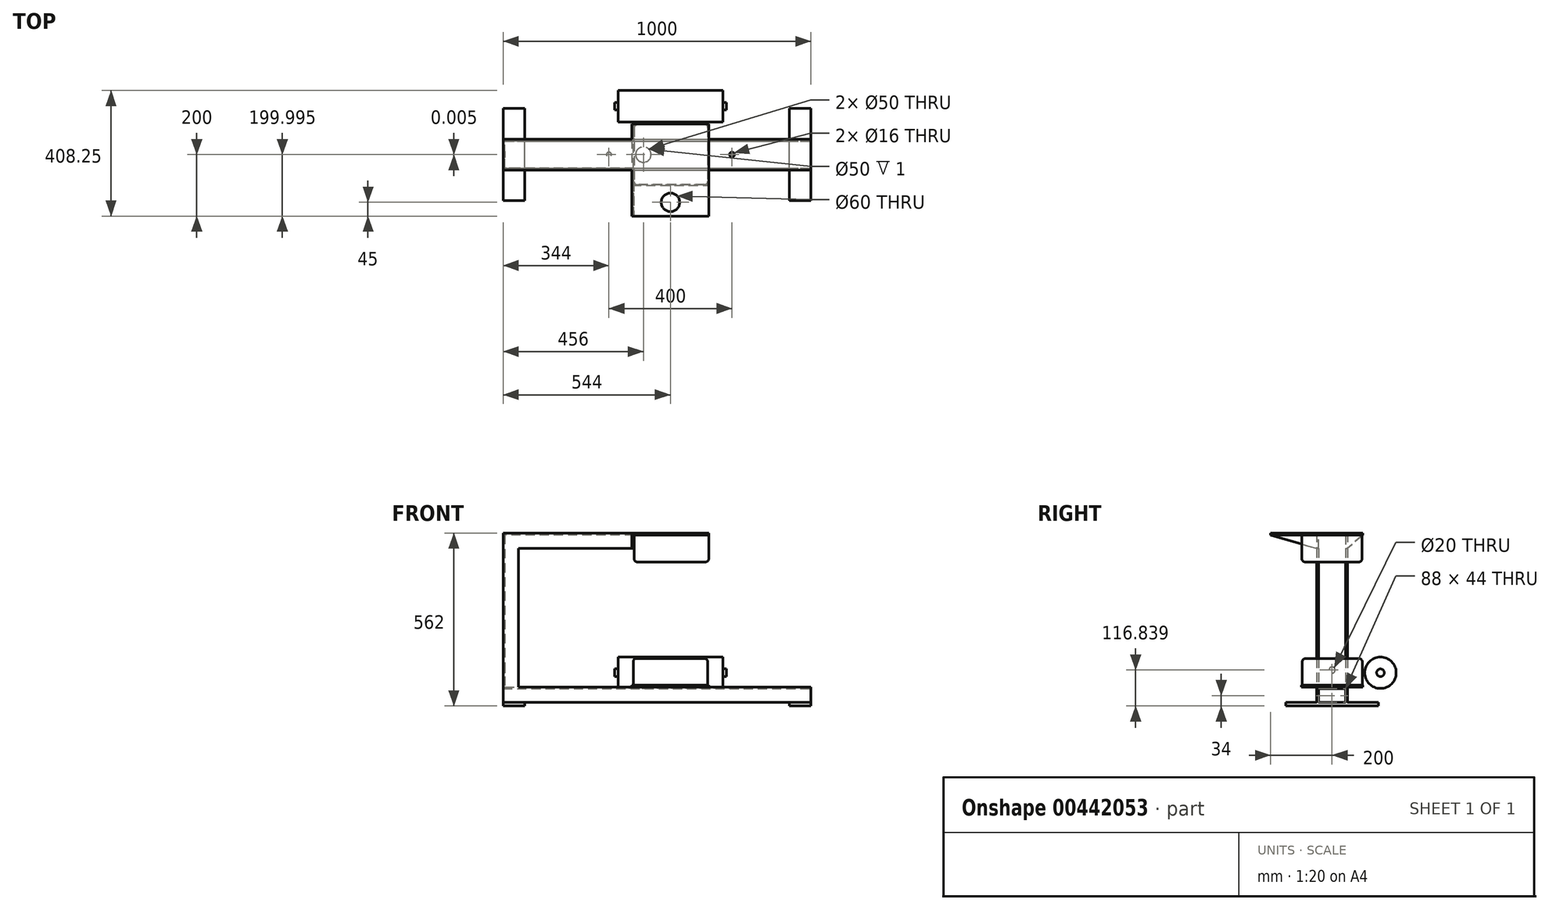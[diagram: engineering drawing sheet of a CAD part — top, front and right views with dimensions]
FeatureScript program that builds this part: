
annotation { "Feature Type Name" : "Feature", "Feature Type Description" : "" }
export const myFeature = defineFeature(function(context is Context, id is Id, definition is map)
    precondition{}
    {
        {
            var Q0;
            Q0=qCreatedBy(makeId("Right.planeOp"),FACE);
            var sketch = newSketch(context, id + "F0", { "sketchPlane" : qUnion([Q0])});
            skLineSegment(sketch, "E0", {"start": v(50, 0) * mm, "end": v(50, 50) * mm});
            skLineSegment(sketch, "E1", {"start": v(50, 50) * mm, "end": v(-50, 50) * mm});
            skLineSegment(sketch, "E2", {"start": v(-50, 50) * mm, "end": v(-50, 0) * mm});
            skLineSegment(sketch, "E3", {"start": v(-50, 0) * mm, "end": v(-44, 0) * mm});
            skLineSegment(sketch, "E4", {"start": v(-44, 0) * mm, "end": v(-44, 44) * mm});
            skLineSegment(sketch, "E5", {"start": v(-44, 44) * mm, "end": v(44, 44) * mm});
            skLineSegment(sketch, "E6", {"start": v(44, 44) * mm, "end": v(44, 0) * mm});
            skLineSegment(sketch, "E7", {"start": v(44, 0) * mm, "end": v(50, 0) * mm});
            skSolve(sketch);
        }
        {
            var Q0;
            Q0 = qSketchRegion(id + "F0", true);
            extrude(context, id + "F1", {"entities" : qUnion([Q0]), "oppositeDirection" : true, "depth" : 1000 * mm});
        }
        {
            var Q0;
            Q0=makeQuery(id+"F1.opExtrude","SWEPT_FACE",FACE,{"disambiguationData":[OSD([sQuery(id+"F0.wireOp",EDGE,"E1")])]});
            var sketch = newSketch(context, id + "F2", { "sketchPlane" : qUnion([Q0])});
            skLineSegment(sketch, "E8", {"start": v(-1000, 50) * mm, "end": v(-1000, -50) * mm});
            skLineSegment(sketch, "E9", {"start": v(-1000, -50) * mm, "end": v(-950, -50) * mm});
            skLineSegment(sketch, "E10", {"start": v(-950, -50) * mm, "end": v(-950, -44) * mm});
            skLineSegment(sketch, "E11", {"start": v(-950, -44) * mm, "end": v(-994, -44) * mm});
            skLineSegment(sketch, "E12", {"start": v(-994, -44) * mm, "end": v(-994, 44) * mm});
            skLineSegment(sketch, "E13", {"start": v(-994, 44) * mm, "end": v(-950, 44) * mm});
            skLineSegment(sketch, "E14", {"start": v(-950, 44) * mm, "end": v(-950, 50) * mm});
            skLineSegment(sketch, "E15", {"start": v(-950, 50) * mm, "end": v(-1000, 50) * mm});
            skSolve(sketch);
        }
        {
            var Q0;
            Q0=makeQuery(id+"F2.imprint","IMPRINT",FACE,{"disambiguationData":[TD([[makeQuery(id+"F2.imprint","IMPRINT",EDGE,{"derivedFrom":sQuery(id+"F2.wireOp",EDGE,"E8")}),1.0]])]});
            extrude(context, id + "F3", {"entities" : qUnion([Q0]), "operationType" : NewBodyOperationType.ADD, "depth" : 500 * mm});
        }
        {
            var Q0;
            Q0=makeQuery(id+"F3.opExtrude","SWEPT_FACE",FACE,{"disambiguationData":[OSD([sQuery(id+"F2.wireOp",EDGE,"E14")])]});
            var sketch = newSketch(context, id + "F4", { "sketchPlane" : qUnion([Q0])});
            skLineSegment(sketch, "E16", {"start": v(50, 550) * mm, "end": v(-50, 550) * mm});
            skLineSegment(sketch, "E17", {"start": v(-50, 550) * mm, "end": v(-50, 500) * mm});
            skLineSegment(sketch, "E18", {"start": v(-50, 500) * mm, "end": v(-44, 500) * mm});
            skLineSegment(sketch, "E19", {"start": v(-44, 500) * mm, "end": v(-44, 544) * mm});
            skLineSegment(sketch, "E20", {"start": v(-44, 544) * mm, "end": v(44, 544) * mm});
            skLineSegment(sketch, "E21", {"start": v(44, 544) * mm, "end": v(44, 500) * mm});
            skLineSegment(sketch, "E22", {"start": v(44, 500) * mm, "end": v(50, 500) * mm});
            skLineSegment(sketch, "E23", {"start": v(50, 500) * mm, "end": v(50, 550) * mm});
            skSolve(sketch);
        }
        {
            var Q0;
            Q0 = qSketchRegion(id + "F4", true);
            extrude(context, id + "F5", {"entities" : qUnion([Q0]), "operationType" : NewBodyOperationType.ADD, "depth" : 369 * mm, "hasSecondDirection" : true, "secondDirectionOppositeDirection" : true, "secondDirectionDepth" : 50 * mm});
        }
        {
            var Q0;
            Q0=makeQuery(id+"F5.opExtrude","CAP_FACE",FACE,{"disambiguationData":[OSD([sQuery(id+"F4.wireOp",EDGE,"E16"),sQuery(id+"F4.wireOp",EDGE,"E17"),sQuery(id+"F4.wireOp",EDGE,"E18"),sQuery(id+"F4.wireOp",EDGE,"E19"),sQuery(id+"F4.wireOp",EDGE,"E20"),sQuery(id+"F4.wireOp",EDGE,"E21"),sQuery(id+"F4.wireOp",EDGE,"E22"),sQuery(id+"F4.wireOp",EDGE,"E23")])],"isStart":false});
            var sketch = newSketch(context, id + "F6", { "sketchPlane" : qUnion([Q0])});
            skLineSegment(sketch, "E24", {"start": v(0, 550) * mm, "end": v(100, 550) * mm});
            skLineSegment(sketch, "E25", {"start": v(100, 550) * mm, "end": v(100, 544) * mm});
            skLineSegment(sketch, "E26", {"start": v(100, 544) * mm, "end": v(-200, 544) * mm});
            skLineSegment(sketch, "E27", {"start": v(-200, 544) * mm, "end": v(-200, 550) * mm});
            skLineSegment(sketch, "E28", {"start": v(-200, 550) * mm, "end": v(0, 550) * mm});
            skSolve(sketch);
        }
        {
            var Q0;
            Q0 = qSketchRegion(id + "F6", true);
            extrude(context, id + "F7", {"entities" : qUnion([Q0]), "operationType" : NewBodyOperationType.ADD, "depth" : 250 * mm});
        }
        {
            var Q0;
            {var subQ0=sQuery(id+"F4.wireOp",EDGE,"E17");var subQ2=sQuery(id+"F4.wireOp",EDGE,"E18");var subQ3=sQuery(id+"F4.wireOp",EDGE,"E19");var subQ4=sQuery(id+"F4.wireOp",EDGE,"E20");Q0=makeQuery(id+"F7.boolean.opBoolean","SPLIT",FACE,{"disambiguationData":[TD([makeQuery(id+"F1.opExtrude","SWEPT_FACE",FACE,{"disambiguationData":[OSD([sQuery(id+"F0.wireOp",EDGE,"E2")])]})])],"derivedFrom":makeQuery(id+"F5.opExtrude","CAP_FACE",FACE,{"disambiguationData":[OSD([sQuery(id+"F4.wireOp",EDGE,"E16"),subQ0,subQ2,subQ3,subQ4,sQuery(id+"F4.wireOp",EDGE,"E21"),sQuery(id+"F4.wireOp",EDGE,"E22"),sQuery(id+"F4.wireOp",EDGE,"E23")])],"isStart":false})});}
            var sketch = newSketch(context, id + "F8", { "sketchPlane" : qUnion([Q0])});
            skLineSegment(sketch, "E29", {"start": v(-44, 544) * mm, "end": v(-200, 544) * mm});
            skLineSegment(sketch, "E30", {"start": v(-200, 544) * mm, "end": v(-50, 500) * mm});
            skLineSegment(sketch, "E31", {"start": v(-50, 500) * mm, "end": v(-44, 500) * mm});
            skLineSegment(sketch, "E32", {"start": v(-44, 544) * mm, "end": v(-44, 500) * mm});
            skSolve(sketch);
        }
        {
            var Q0;
            Q0 = qSketchRegion(id + "F8", true);
            extrude(context, id + "F9", {"entities" : qUnion([Q0]), "operationType" : NewBodyOperationType.ADD, "depth" : 6 * mm});
        }
        {
            var Q0;
            {var subQ0=sQuery(id+"F4.wireOp",EDGE,"E20");var subQ2=sQuery(id+"F4.wireOp",EDGE,"E21");var subQ3=sQuery(id+"F4.wireOp",EDGE,"E22");var subQ4=sQuery(id+"F4.wireOp",EDGE,"E23");Q0=makeQuery(id+"F7.boolean.opBoolean","SPLIT",FACE,{"disambiguationData":[TD([makeQuery(id+"F1.opExtrude","SWEPT_FACE",FACE,{"disambiguationData":[OSD([sQuery(id+"F0.wireOp",EDGE,"E0")])]})])],"derivedFrom":makeQuery(id+"F5.opExtrude","CAP_FACE",FACE,{"disambiguationData":[OSD([sQuery(id+"F4.wireOp",EDGE,"E16"),sQuery(id+"F4.wireOp",EDGE,"E17"),sQuery(id+"F4.wireOp",EDGE,"E18"),sQuery(id+"F4.wireOp",EDGE,"E19"),subQ0,subQ2,subQ3,subQ4])],"isStart":false})});}
            var sketch = newSketch(context, id + "F10", { "sketchPlane" : qUnion([Q0])});
            skLineSegment(sketch, "E33", {"start": v(44, 544) * mm, "end": v(100, 544) * mm});
            skLineSegment(sketch, "E34", {"start": v(100, 544) * mm, "end": v(50, 500) * mm});
            skLineSegment(sketch, "E35", {"start": v(50, 500) * mm, "end": v(44, 500) * mm});
            skLineSegment(sketch, "E36", {"start": v(44, 500) * mm, "end": v(44, 544) * mm});
            skSolve(sketch);
        }
        {
            var Q0;
            Q0 = qSketchRegion(id + "F10", true);
            extrude(context, id + "F11", {"entities" : qUnion([Q0]), "operationType" : NewBodyOperationType.ADD, "depth" : 6 * mm});
        }
        {
            var Q0;
            Q0=makeQuery(id+"F3.boolean.opBoolean","MERGE",FACE,{"derivedFrom":[makeQuery(id+"F1.opExtrude","CAP_FACE",FACE,{"disambiguationData":[OSD([sQuery(id+"F0.wireOp",EDGE,"E0"),sQuery(id+"F0.wireOp",EDGE,"E1"),sQuery(id+"F0.wireOp",EDGE,"E2"),sQuery(id+"F0.wireOp",EDGE,"E3"),sQuery(id+"F0.wireOp",EDGE,"E4"),sQuery(id+"F0.wireOp",EDGE,"E5"),sQuery(id+"F0.wireOp",EDGE,"E6"),sQuery(id+"F0.wireOp",EDGE,"E7")])],"isStart":false}),makeQuery(id+"F3.opExtrude","SWEPT_FACE",FACE,{"disambiguationData":[OSD([sQuery(id+"F2.wireOp",EDGE,"E8")])]})]});
            var sketch = newSketch(context, id + "F12", { "sketchPlane" : qUnion([Q0])});
            skCircle(sketch, "E37", {"center": v(0, 104.84) * mm, "radius": 10 * mm});
            skSolve(sketch);
        }
        {
            var Q0;
            Q0=makeQuery(id+"F12.imprint","IMPRINT",FACE,{"disambiguationData":[TD([[makeQuery(id+"F12.imprint","IMPRINT",EDGE,{"derivedFrom":sQuery(id+"F12.wireOp",EDGE,"E37")}),1.0]])]});
            extrude(context, id + "F13", {"entities" : qUnion([Q0]), "operationType" : NewBodyOperationType.REMOVE, "endBound" : BoundingType.THROUGH_ALL, "oppositeDirection" : true, "depth" : 25 * mm});
        }
        {
            var Q0;
            Q0=makeQuery(id+"F1.opExtrude","SWEPT_FACE",FACE,{"disambiguationData":[OSD([sQuery(id+"F0.wireOp",EDGE,"E1")])]});
            var sketch = newSketch(context, id + "F14", { "sketchPlane" : qUnion([Q0])});
            skCircle(sketch, "E38", {"center": v(-544, 0) * mm, "radius": 25 * mm});
            skLineSegment(sketch, "E39", {"start": v(-994, 0) * mm, "end": v(-544, 0) * mm});
            skSolve(sketch);
        }
        {
            var Q0;
            Q0=makeQuery(id+"F14.imprint","IMPRINT",FACE,{"disambiguationData":[TD([[makeQuery(id+"F14.imprint","IMPRINT",EDGE,{"derivedFrom":sQuery(id+"F14.wireOp",EDGE,"E38")}),1.0]])]});
            extrude(context, id + "F15", {"entities" : qUnion([Q0]), "operationType" : NewBodyOperationType.REMOVE, "oppositeDirection" : true, "depth" : 6 * mm});
        }
        {
            var Q0;
            Q0=makeQuery(id+"F7.boolean.opBoolean","MERGE",FACE,{"derivedFrom":[makeQuery(id+"F5.boolean.opBoolean","MERGE",FACE,{"derivedFrom":[makeQuery(id+"F3.opExtrude","CAP_FACE",FACE,{"disambiguationData":[OSD([sQuery(id+"F2.wireOp",EDGE,"E8"),sQuery(id+"F2.wireOp",EDGE,"E9"),sQuery(id+"F2.wireOp",EDGE,"E10"),sQuery(id+"F2.wireOp",EDGE,"E11"),sQuery(id+"F2.wireOp",EDGE,"E12"),sQuery(id+"F2.wireOp",EDGE,"E13"),sQuery(id+"F2.wireOp",EDGE,"E14"),sQuery(id+"F2.wireOp",EDGE,"E15")])],"isStart":false}),makeQuery(id+"F5.opExtrude","SWEPT_FACE",FACE,{"disambiguationData":[OSD([sQuery(id+"F4.wireOp",EDGE,"E16")])]})]}),makeQuery(id+"F7.opExtrude","SWEPT_FACE",FACE,{"disambiguationData":[OSD([sQuery(id+"F6.wireOp",EDGE,"E24"),sQuery(id+"F6.wireOp",EDGE,"E28")])]})]});
            var sketch = newSketch(context, id + "F16", { "sketchPlane" : qUnion([Q0])});
            skCircle(sketch, "E40", {"center": v(-456, -155) * mm, "radius": 30 * mm});
            skLineSegment(sketch, "E41", {"start": v(-456, -200) * mm, "end": v(-456, -155) * mm});
            skSolve(sketch);
        }
        {
            var Q0;
            Q0=makeQuery(id+"F16.imprint","IMPRINT",FACE,{"disambiguationData":[TD([[makeQuery(id+"F16.imprint","IMPRINT",EDGE,{"derivedFrom":sQuery(id+"F16.wireOp",EDGE,"E40")}),1.0]])]});
            extrude(context, id + "F17", {"entities" : qUnion([Q0]), "operationType" : NewBodyOperationType.REMOVE, "endBound" : BoundingType.THROUGH_ALL, "oppositeDirection" : true, "depth" : 25 * mm});
        }
        {
            var Q0;
            Q0=makeQuery(id+"F1.opExtrude","SWEPT_FACE",FACE,{"disambiguationData":[OSD([sQuery(id+"F0.wireOp",EDGE,"E1")])]});
            var sketch = newSketch(context, id + "F18", { "sketchPlane" : qUnion([Q0])});
            skLineSegment(sketch, "E42", {"start": v(-556, 100) * mm, "end": v(-556, 50) * mm});
            skLineSegment(sketch, "E43", {"start": v(-331, -100.18) * mm, "end": v(-331, 99.82) * mm});
            skLineSegment(sketch, "E44", {"start": v(-331, 99.82) * mm, "end": v(-581, 99.82) * mm});
            skLineSegment(sketch, "E45", {"start": v(-581, 99.82) * mm, "end": v(-581, -100.18) * mm});
            skLineSegment(sketch, "E46", {"start": v(-581, -100.18) * mm, "end": v(-331, -100.18) * mm});
            skLineSegment(sketch, "E47", {"start": v(-950, -50) * mm, "end": v(-581, -50) * mm});
            skSolve(sketch);
        }
        {
            var Q0;
            Q0 = qSketchRegion(id + "F18", true);
            extrude(context, id + "F19", {"entities" : qUnion([Q0]), "operationType" : NewBodyOperationType.ADD, "depth" : 6 * mm});
        }
        {
            var Q0;
            Q0=makeQuery(id+"F1.opExtrude","SWEPT_FACE",FACE,{"disambiguationData":[OSD([sQuery(id+"F0.wireOp",EDGE,"E3")])]});
            var sketch = newSketch(context, id + "F20", { "sketchPlane" : qUnion([Q0])});
            skLineSegment(sketch, "E48", {"start": v(-1000, 50) * mm, "end": v(-1000, 150) * mm});
            skLineSegment(sketch, "E49", {"start": v(-1000, 150) * mm, "end": v(-930, 150) * mm});
            skLineSegment(sketch, "E50", {"start": v(-930, 150) * mm, "end": v(-930, -150) * mm});
            skLineSegment(sketch, "E51", {"start": v(-930, -150) * mm, "end": v(-1000, -150) * mm});
            skLineSegment(sketch, "E52", {"start": v(-1000, -150) * mm, "end": v(-1000, 50) * mm});
            skLineSegment(sketch, "E53", {"start": v(0, 50) * mm, "end": v(0, 150) * mm});
            skLineSegment(sketch, "E54", {"start": v(0, 150) * mm, "end": v(-70, 150) * mm});
            skLineSegment(sketch, "E55", {"start": v(-70, 150) * mm, "end": v(-70, -150) * mm});
            skLineSegment(sketch, "E56", {"start": v(-70, -150) * mm, "end": v(0, -150) * mm});
            skLineSegment(sketch, "E57", {"start": v(0, -150) * mm, "end": v(0, 50) * mm});
            skSolve(sketch);
        }
        {
            var Q0;
            Q0 = qSketchRegion(id + "F20", true);
            extrude(context, id + "F21", {"entities" : qUnion([Q0]), "operationType" : NewBodyOperationType.ADD, "depth" : 12 * mm});
        }
        {
            var Q0;
            Q0=makeQuery(id+"F19.boolean.opBoolean","SPLIT",FACE,{"disambiguationData":[TD([makeQuery(id+"F3.opExtrude","SWEPT_FACE",FACE,{"disambiguationData":[OSD([sQuery(id+"F2.wireOp",EDGE,"E10")])]})])],"derivedFrom":makeQuery(id+"F1.opExtrude","SWEPT_FACE",FACE,{"disambiguationData":[OSD([sQuery(id+"F0.wireOp",EDGE,"E1")])]})});
            var sketch = newSketch(context, id + "F22", { "sketchPlane" : qUnion([Q0])});
            skPoint(sketch, "E58.endSnap0", {"position": v(-994, 0) * mm});
            skLineSegment(sketch, "E59", {"start": v(0, 0) * mm, "end": v(-256, 0) * mm});
            skLineSegment(sketch, "E60", {"start": v(-256, 0) * mm, "end": v(-656, 0) * mm});
            skPoint(sketch, "E60.endSnap0", {"position": v(-581, 0) * mm});
            skCircle(sketch, "E61", {"center": v(-656, 0) * mm, "radius": 8 * mm});
            skCircle(sketch, "E62", {"center": v(-256, 0) * mm, "radius": 8 * mm});
            skSolve(sketch);
        }
        {
            var Q0;
            Q0 = qSketchRegion(id + "F22", true);
            extrude(context, id + "F23", {"entities" : qUnion([Q0]), "operationType" : NewBodyOperationType.REMOVE, "oppositeDirection" : true, "depth" : 6 * mm});
        }
        {
            var Q0;
            Q0=qCreatedBy(makeId("Top.planeOp"),FACE);
            var sketch = newSketch(context, id + "F24", { "sketchPlane" : qUnion([Q0])});
            skLineSegment(sketch, "E63", {"start": v(93.08, 453.86) * mm, "end": v(288.08, 453.86) * mm});
            skLineSegment(sketch, "E64", {"start": v(288.08, 453.86) * mm, "end": v(288.08, 211.86) * mm});
            skLineSegment(sketch, "E65", {"start": v(288.08, 211.86) * mm, "end": v(93.08, 211.86) * mm});
            skLineSegment(sketch, "E66", {"start": v(93.08, 211.86) * mm, "end": v(93.08, 453.86) * mm});
            skSolve(sketch);
        }
        {
            var Q0;
            Q0 = qSketchRegion(id + "F24", true);
            extrude(context, id + "F25", {"entities" : qUnion([Q0]), "depth" : 87 * mm});
        }
        {
            var Q0;
            Q0=makeQuery(id+"F25.opExtrude","CAP_EDGE",EDGE,{"disambiguationData":[OSD([sQuery(id+"F24.wireOp",EDGE,"E64")])],"isStart":false});
            var Q1;
            Q1=makeQuery(id+"F25.opExtrude","CAP_EDGE",EDGE,{"disambiguationData":[OSD([sQuery(id+"F24.wireOp",EDGE,"E66")])],"isStart":false});
            var Q2;
            Q2=makeQuery(id+"F25.opExtrude","CAP_EDGE",EDGE,{"disambiguationData":[OSD([sQuery(id+"F24.wireOp",EDGE,"E65")])],"isStart":false});
            var Q3;
            Q3=makeQuery(id+"F25.opExtrude","CAP_EDGE",EDGE,{"disambiguationData":[OSD([sQuery(id+"F24.wireOp",EDGE,"E63")])],"isStart":false});
            var Q4;
            Q4=makeQuery(id+"F25.opExtrude","SWEPT_EDGE",EDGE,{"disambiguationData":[OSD([sQuery(id+"F24.wireOp",EDGE,"E63"),sQuery(id+"F24.wireOp",EDGE,"E64")])]});
            var Q5;
            Q5=makeQuery(id+"F25.opExtrude","SWEPT_EDGE",EDGE,{"disambiguationData":[OSD([sQuery(id+"F24.wireOp",EDGE,"E64"),sQuery(id+"F24.wireOp",EDGE,"E65")])]});
            var Q6;
            Q6=makeQuery(id+"F25.opExtrude","SWEPT_EDGE",EDGE,{"disambiguationData":[OSD([sQuery(id+"F24.wireOp",EDGE,"E65"),sQuery(id+"F24.wireOp",EDGE,"E66")])]});
            var Q7;
            Q7=makeQuery(id+"F25.opExtrude","SWEPT_EDGE",EDGE,{"disambiguationData":[OSD([sQuery(id+"F24.wireOp",EDGE,"E63"),sQuery(id+"F24.wireOp",EDGE,"E66")])]});
            fillet(context, id + "F26", {"entities" : qUnion([Q0, Q1, Q2, Q3, Q4, Q5, Q6, Q7]), "radius" : 10 * mm, "tangentPropagation" : true, "allowEdgeOverflow" : false});
        }
        {
            var Q0;
            Q0=makeQuery(id+"F25.opExtrude","SWEPT_BODY",BODY,{"disambiguationData":[OSD([sQuery(id+"F24.wireOp",EDGE,"E63"),sQuery(id+"F24.wireOp",EDGE,"E64"),sQuery(id+"F24.wireOp",EDGE,"E65"),sQuery(id+"F24.wireOp",EDGE,"E66")])]});
            transform(context, id + "F27", {"entities" : qUnion([Q0]), "transformType" : TransformType.TRANSLATION_3D, "dx" : -646 * mm, "dy" : -333 * mm, "dz" : 55 * mm, "makeCopy" : true});
        }
        {
            var Q0;
            Q0=makeQuery(id+"F25.opExtrude","SWEPT_BODY",BODY,{"disambiguationData":[OSD([sQuery(id+"F24.wireOp",EDGE,"E63"),sQuery(id+"F24.wireOp",EDGE,"E64"),sQuery(id+"F24.wireOp",EDGE,"E65"),sQuery(id+"F24.wireOp",EDGE,"E66")])]});
            transform(context, id + "F28", {"entities" : qUnion([Q0]), "transformType" : TransformType.TRANSLATION_3D, "dx" : -454 * mm, "dy" : 0 * mm, "dz" : 418 * mm, "makeCopy" : false});
        }
        {
            var Q0;
            Q0=makeQuery(id+"F25.opExtrude","SWEPT_BODY",BODY,{"disambiguationData":[OSD([sQuery(id+"F24.wireOp",EDGE,"E63"),sQuery(id+"F24.wireOp",EDGE,"E64"),sQuery(id+"F24.wireOp",EDGE,"E65"),sQuery(id+"F24.wireOp",EDGE,"E66")])]});
            var Q1;
            Q1=makeQuery(id+"F25.opExtrude","CAP_EDGE",EDGE,{"disambiguationData":[OSD([sQuery(id+"F24.wireOp",EDGE,"E65")])],"isStart":true});
            transform(context, id + "F29", {"entities" : qUnion([Q0]), "transformType" : TransformType.ROTATION, "transformAxis" : qUnion([Q1]), "angle" : 180 * degree, "makeCopy" : false});
        }
        {
            var Q0;
            Q0=makeQuery(id+"F25.opExtrude","SWEPT_BODY",BODY,{"disambiguationData":[OSD([sQuery(id+"F24.wireOp",EDGE,"E63"),sQuery(id+"F24.wireOp",EDGE,"E64"),sQuery(id+"F24.wireOp",EDGE,"E65"),sQuery(id+"F24.wireOp",EDGE,"E66")])]});
            transform(context, id + "F30", {"entities" : qUnion([Q0]), "transformType" : TransformType.TRANSLATION_3D, "dx" : -193 * mm, "dy" : -92 * mm, "dz" : 125 * mm, "makeCopy" : false});
        }
        {
            var Q0;
            Q0=qCreatedBy(makeId("Right.planeOp"),FACE);
            cPlane(context, id + "F31", {"entities" : qUnion([Q0]), "cplaneType" : CPlaneType.OFFSET, "offset" : 456 * mm, "oppositeDirection" : true, "width" : 150 * mm, "height" : 150 * mm});
        }
        {
            var Q0;
            Q0=qCreatedBy(id+"F31.planeOp",FACE);
            var sketch = newSketch(context, id + "F32", { "sketchPlane" : qUnion([Q0])});
            skLineSegment(sketch, "E67", {"start": v(0, -106.93) * mm, "end": v(0, 589) * mm, "construction": true});
            skSolve(sketch);
        }
        {
            var Q0;
            Q0=makeQuery(id+"F25.opExtrude","SWEPT_BODY",BODY,{"disambiguationData":[OSD([sQuery(id+"F24.wireOp",EDGE,"E63"),sQuery(id+"F24.wireOp",EDGE,"E64"),sQuery(id+"F24.wireOp",EDGE,"E65"),sQuery(id+"F24.wireOp",EDGE,"E66")])]});
            var Q1;
            Q1=sQuery(id+"F32.wireOp",EDGE,"E67");
            transform(context, id + "F33", {"entities" : qUnion([Q0]), "transformType" : TransformType.ROTATION, "transformAxis" : qUnion([Q1]), "angle" : 90 * degree, "makeCopy" : false});
        }
        {
            var Q0;
            Q0=makeQuery(id+"F27.opPattern","COPY",BODY,{"derivedFrom":makeQuery(id+"F25.opExtrude","SWEPT_BODY",BODY,{"disambiguationData":[OSD([sQuery(id+"F24.wireOp",EDGE,"E63"),sQuery(id+"F24.wireOp",EDGE,"E64"),sQuery(id+"F24.wireOp",EDGE,"E65"),sQuery(id+"F24.wireOp",EDGE,"E66")])]}),"instanceName":"1"});
            var Q1;
            Q1=sQuery(id+"F32.wireOp",EDGE,"E67");
            transform(context, id + "F34", {"entities" : qUnion([Q0]), "transformType" : TransformType.ROTATION, "transformAxis" : qUnion([Q1]), "angle" : 90 * degree, "makeCopy" : false});
        }
        {
            var Q0;
            Q0=makeQuery(id+"F25.opExtrude","SWEPT_BODY",BODY,{"disambiguationData":[OSD([sQuery(id+"F24.wireOp",EDGE,"E63"),sQuery(id+"F24.wireOp",EDGE,"E64"),sQuery(id+"F24.wireOp",EDGE,"E65"),sQuery(id+"F24.wireOp",EDGE,"E66")])]});
            transform(context, id + "F35", {"entities" : qUnion([Q0]), "transformType" : TransformType.TRANSLATION_3D, "dx" : 2 * mm, "dy" : 0 * mm, "dz" : 0 * mm, "makeCopy" : false});
        }
        {
            var Q0;
            {var subQ0=sQuery(id+"F18.wireOp",EDGE,"E43");var subQ1=sQuery(id+"F18.wireOp",EDGE,"E45");var subQ2=sQuery(id+"F18.wireOp",EDGE,"E46");Q0=makeQuery(id+"F19.boolean.opBoolean","SPLIT",FACE,{"disambiguationData":[TD([makeQuery(id+"F1.opExtrude","SWEPT_FACE",FACE,{"disambiguationData":[OSD([sQuery(id+"F0.wireOp",EDGE,"E2")])]})])],"derivedFrom":makeQuery(id+"F19.opExtrude","CAP_FACE",FACE,{"disambiguationData":[OSD([subQ0,sQuery(id+"F18.wireOp",EDGE,"E44"),subQ1,subQ2])],"isStart":true})});}
            var sketch = newSketch(context, id + "F36", { "sketchPlane" : qUnion([Q0])});
            skLineSegment(sketch, "E68", {"start": v(0, 0) * mm, "end": v(-11.87, 0) * mm});
            skCircle(sketch, "E69", {"center": v(-544, 0) * mm, "radius": 25 * mm});
            skLineSegment(sketch, "E70", {"start": v(0, 0) * mm, "end": v(-544, 0) * mm});
            skSolve(sketch);
        }
        {
            var Q0;
            Q0 = qSketchRegion(id + "F36", true);
            extrude(context, id + "F37", {"entities" : qUnion([Q0]), "operationType" : NewBodyOperationType.REMOVE, "oppositeDirection" : true, "depth" : 6 * mm});
        }
        {
            var Q0;
            Q0=qCreatedBy(makeId("Right.planeOp"),FACE);
            var sketch = newSketch(context, id + "F38", { "sketchPlane" : qUnion([Q0])});
            skCircle(sketch, "E71", {"center": v(213.25, 96.1) * mm, "radius": 51 * mm});
            skSolve(sketch);
        }
        {
            var Q0;
            Q0=makeQuery(id+"F38.imprint","IMPRINT",FACE,{"disambiguationData":[TD([[makeQuery(id+"F38.imprint","IMPRINT",EDGE,{"derivedFrom":sQuery(id+"F38.wireOp",EDGE,"E71")}),1.0]])]});
            extrude(context, id + "F39", {"entities" : qUnion([Q0]), "depth" : 340 * mm});
        }
        {
            var Q0;
            Q0=makeQuery(id+"F39.opExtrude","CAP_FACE",FACE,{"disambiguationData":[OSD([sQuery(id+"F38.wireOp",EDGE,"E71")])],"isStart":false});
            var sketch = newSketch(context, id + "F40", { "sketchPlane" : qUnion([Q0])});
            skCircle(sketch, "E72", {"center": v(213.25, 96.1) * mm, "radius": 12.5 * mm});
            skSolve(sketch);
        }
        {
            var Q0;
            Q0=makeQuery(id+"F40.imprint","IMPRINT",FACE,{"disambiguationData":[TD([[makeQuery(id+"F40.imprint","IMPRINT",EDGE,{"derivedFrom":sQuery(id+"F40.wireOp",EDGE,"E72")}),1.0]])]});
            extrude(context, id + "F41", {"entities" : qUnion([Q0]), "operationType" : NewBodyOperationType.ADD, "depth" : 12 * mm});
        }
        {
            var Q0;
            Q0=makeQuery(id+"F39.opExtrude","CAP_FACE",FACE,{"disambiguationData":[OSD([sQuery(id+"F38.wireOp",EDGE,"E71")])],"isStart":true});
            var sketch = newSketch(context, id + "F42", { "sketchPlane" : qUnion([Q0])});
            skCircle(sketch, "E73", {"center": v(-213.25, 96.1) * mm, "radius": 12.5 * mm});
            skSolve(sketch);
        }
        {
            var Q0;
            Q0=makeQuery(id+"F42.imprint","IMPRINT",FACE,{"disambiguationData":[TD([[makeQuery(id+"F42.imprint","IMPRINT",EDGE,{"derivedFrom":sQuery(id+"F42.wireOp",EDGE,"E73")}),1.0]])]});
            extrude(context, id + "F43", {"entities" : qUnion([Q0]), "operationType" : NewBodyOperationType.ADD, "depth" : 12 * mm});
        }
        {
            var Q0;
            Q0=makeQuery(id+"F39.opExtrude","SWEPT_BODY",BODY,{"disambiguationData":[OSD([sQuery(id+"F38.wireOp",EDGE,"E71")])]});
            transform(context, id + "F44", {"entities" : qUnion([Q0]), "transformType" : TransformType.TRANSLATION_3D, "dx" : -625 * mm, "dy" : -56 * mm, "dz" : 0 * mm, "makeCopy" : false});
        }
        {
            var Q0;
            Q0=makeQuery(id+"F39.opExtrude","SWEPT_BODY",BODY,{"disambiguationData":[OSD([sQuery(id+"F38.wireOp",EDGE,"E71")])]});
            transform(context, id + "F45", {"entities" : qUnion([Q0]), "transformType" : TransformType.TRANSLATION_3D, "dx" : -1 * mm, "dy" : 0 * mm, "dz" : 0 * mm, "makeCopy" : false});
        }
    });
